# Revit family: RN 80054 Optipress-Aquaplus-Gomito
name_source: partatom
category: Rohrformteile
units: mm (PartAtom-declared; Revit-internal decimal feet)

## family parameters
Arbeitsebenenbasiert = Nein
Beim Laden mit Abzugskörper schneiden = Nein
Bemaßung runder Anschluss = Durchmesser verwenden
Gemeinsam genutzt = Nein
Immer vertikal = Ja
Teiletyp = Nicht definiert

## types (4) — shared parameters
1.010.00.2 Number of the part of the guideline = 29
1.010.00.3 Issue date (month) of the guideline = 201308
1.010.00.4 Manufacturer name = R. Nussbaum AG
1.010.00.5 Revision date of the file = 20190521
1.100.00.4 Product designation = Fornitura
1.110.00.2 Index = 4
1.110.00.4 Product designation = Optipress
1.960/3L.00.8 Link (URL) = https://www.nussbaum.ch
29.700.00.4 Product name = Optipress-Aquaplus-Gomito, con flangia murale prolungata
29.700.00.5 Product identification = 2
29.700.00.6 Cross-sectional shape = 1
29.700.00.7 Nominal size system = DN
29.700.00.8 Nominal pressure system = PN
29.710.02.4 Nominal pressure = 16
29.710.02.5 max. allowed overpressure [hPa] = 1600
29.710.02.7 max. allowed continuous operating pressure [hPa] = 1600
29.710.02.9 max. allowed continuous operating temperature [°C] = 95
CONNECTOR0_ref_dX = 45 mm
Connector Visibility = Nein
EnclosingSpace Visibility = Nein

## per-type parameters (varying)
| type | 1.800.00.3 BS number | 1.810.00.3 Manufacturer’s reference number | 1.810.00.4 DATANORM number | 1.810.00.5 StLB number | 1.810.00.6 GTIN number | 29.710.02.10 Fitting weight [kg] | 29.710.02.3 Designation | CONNECTOR0_DIAMETER_dZ_0r | CONNECTOR0_dZ_00 | CONNECTOR0_dZ_01 | CONNECTOR0_ref_dZ | CONNECTOR1_DIAMETER_dX_0r | CONNECTOR1_dX_00 | CONNECTOR1_dX_01 | CONNECTOR1_ref_dX | R. Nussbaum AG 80054.21 it Visibility | R. Nussbaum AG 80054.22 it Visibility | R. Nussbaum AG 80054.24 it Visibility | R. Nussbaum AG 80054.25 it Visibility |
| 80054.21, Optipress-Aquaplus-Gomito, con flangia murale prolungata, DN=12x15, L=44, Rp=½ | 01900400000000000000000000000000000000000000000035000000000000000001 | 80054.21 | 80054.21 | 263.172 | 7612945686770 | 0.145 | Optipress-Aquaplus-Gomito, con flangia murale prolungata, DN=12x15, L=44, Rp=½ | 12 mm  [stored 0.0393701 ft] | 44 mm | 22 mm | 22 mm | 15 mm  [stored 0.0492126 ft] | 52 mm | 65 mm | 52 mm | Ja | Nein | Nein | Nein |
| 80054.22, Optipress-Aquaplus-Gomito, con flangia murale prolungata, DN=15, L=48, Rp=½ | 01900400000000000000000000000000000000000000000035000000000000000002 | 80054.22 | 80054.22 | 263.173 | 7612945686787 | 0.145 | Optipress-Aquaplus-Gomito, con flangia murale prolungata, DN=15, L=48, Rp=½ | 15 mm  [stored 0.0492126 ft] | 48 mm | 26 mm | 26 mm | 15 mm  [stored 0.0492126 ft] | 52 mm | 65 mm | 52 mm | Nein | Ja | Nein | Nein |
| 80054.24, Optipress-Aquaplus-Gomito, con flangia murale prolungata, DN=20x15, L=49, Rp=½ | 01900400000000000000000000000000000000000000000035000000000000000003 | 80054.24 | 80054.24 |  | 7612945686794 | 0.169 | Optipress-Aquaplus-Gomito, con flangia murale prolungata, DN=20x15, L=49, Rp=½ | 20 mm | 49 mm | 25 mm  [stored 0.082021 ft] | 25 mm  [stored 0.082021 ft] | 15 mm  [stored 0.0492126 ft] | 56 mm | 69 mm | 56 mm | Nein | Nein | Ja | Nein |
| 80054.25, Optipress-Aquaplus-Gomito, con flangia murale prolungata, DN=20, L=52, Rp=¾ | 01900400000000000000000000000000000000000000000035000000000000000004 | 80054.25 | 80054.25 | 263.174 | 7612945686800 | 0.212 | Optipress-Aquaplus-Gomito, con flangia murale prolungata, DN=20, L=52, Rp=¾ | 20 mm | 52 mm | 28 mm | 28 mm | 20 mm | 56 mm | 71 mm | 56 mm | Nein | Nein | Nein | Ja |

note: column(s) folded — value = type name in every type: 1.800.00.4 Comment field

note: [stored X ft] marks values corroborated as IEEE doubles in the binary element streams (Revit-internal decimal feet)

## geometry (parser evidence)
native form markers: Sweep x1
no freeform markers — native parametric forms only
